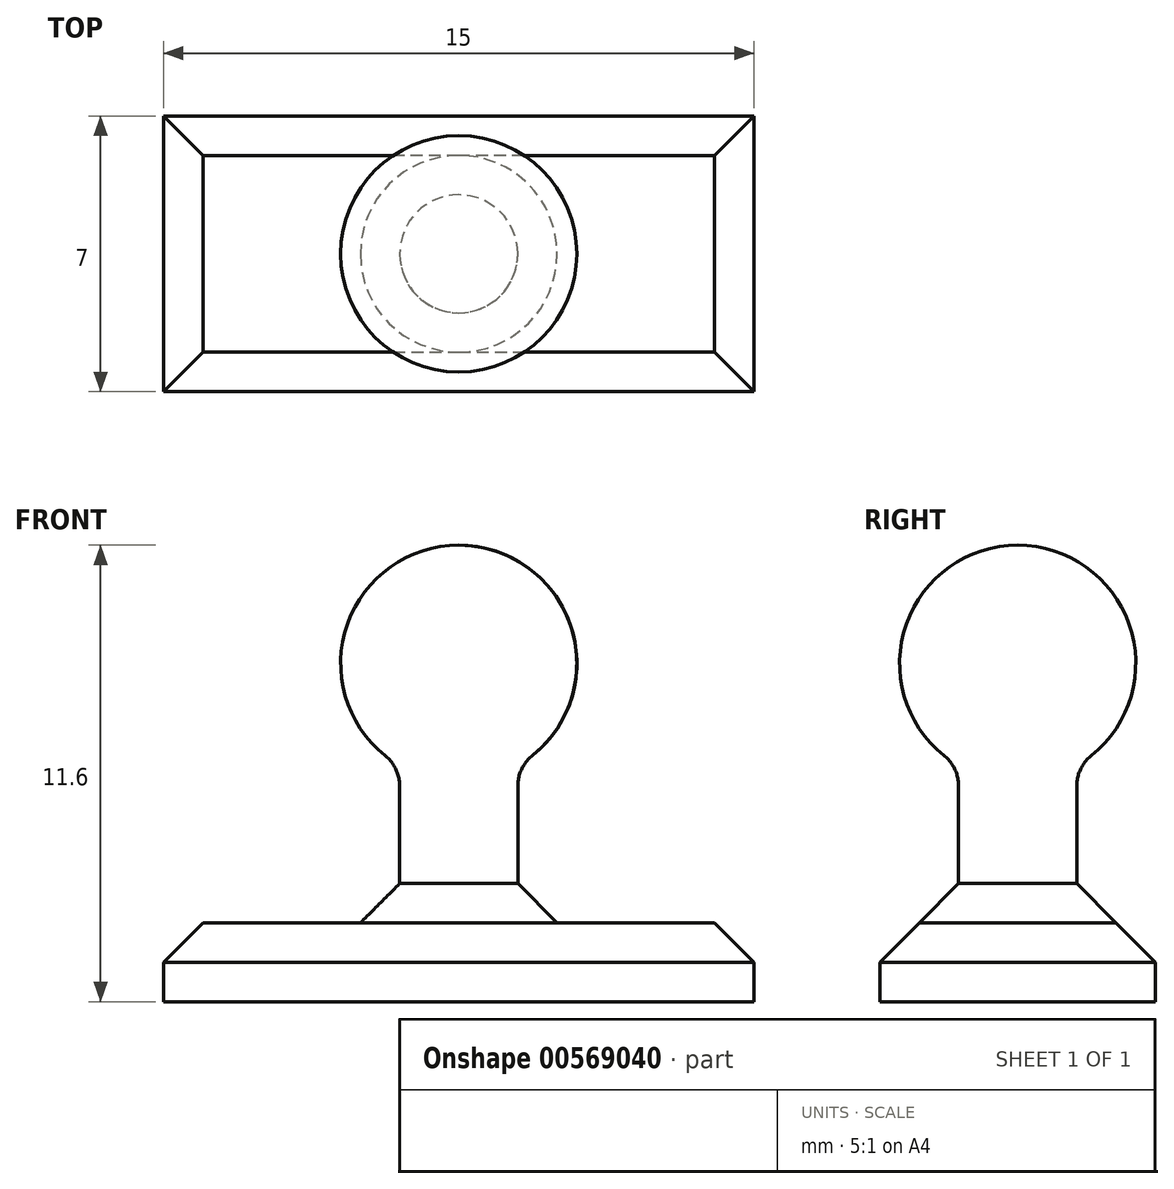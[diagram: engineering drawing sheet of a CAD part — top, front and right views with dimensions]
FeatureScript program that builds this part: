
annotation { "Feature Type Name" : "Feature", "Feature Type Description" : "" }
export const myFeature = defineFeature(function(context is Context, id is Id, definition is map)
    precondition{}
    {
        {
            var Q0;
            Q0=qCreatedBy(makeId("Front.planeOp"),FACE);
            var sketch = newSketch(context, id + "F0", { "sketchPlane" : qUnion([Q0])});
            skLineSegment(sketch, "E0", {"start": v(-1.5, 0) * mm, "end": v(-1.5, 4) * mm});
            skArc(sketch, "E1", {"start": v(0, 9.6) * mm, "mid": v(-2.9, 7.37) * mm, "end": v(-1.5, 4) * mm});
            skLineSegment(sketch, "E2", {"start": v(0, 0) * mm, "end": v(0, 9.6) * mm});
            skLineSegment(sketch, "E3", {"start": v(-1.5, 0) * mm, "end": v(0, 0) * mm});
            skLineSegment(sketch, "E4", {"start": v(0, 24.94) * mm, "end": v(0, -14.58) * mm, "construction": true});
            skSolve(sketch);
        }
        {
            var Q0;
            Q0=makeQuery(id+"F0.imprint","IMPRINT",FACE,{"disambiguationData":[TD([[makeQuery(id+"F0.imprint","IMPRINT",EDGE,{"derivedFrom":sQuery(id+"F0.wireOp",EDGE,"E0")}),-1.0]])]});
            var Q1;
            Q1=sQuery(id+"F0.wireOp",EDGE,"E3");
            var Q2;
            Q2=sQuery(id+"F0.wireOp",EDGE,"E0");
            var Q3;
            Q3=sQuery(id+"F0.wireOp",EDGE,"E1");
            var Q4;
            Q4=sQuery(id+"F0.wireOp",EDGE,"E2");
            revolve(context, id + "F1", {"entities" : qUnion([Q0]), "surfaceEntities" : qUnion([Q1, Q2, Q3]), "axis" : qUnion([Q4]), "revolveType" : RevolveType.FULL});
        }
        {
            var Q0;
            Q0=makeQuery(id+"F1.opRevolve","SWEPT_FACE",FACE,{"disambiguationData":[OSD([sQuery(id+"F0.wireOp",EDGE,"E3")])]});
            var sketch = newSketch(context, id + "F2", { "sketchPlane" : qUnion([Q0])});
            skLineSegment(sketch, "E5.bottom", {"start": v(7.5, 3.5) * mm, "end": v(-7.5, 3.5) * mm});
            skLineSegment(sketch, "E5.top", {"start": v(7.5, -3.5) * mm, "end": v(-7.5, -3.5) * mm});
            skLineSegment(sketch, "E5.left", {"start": v(7.5, 3.5) * mm, "end": v(7.5, -3.5) * mm});
            skLineSegment(sketch, "E5.right", {"start": v(-7.5, 3.5) * mm, "end": v(-7.5, -3.5) * mm});
            skPoint(sketch, "E5.middle", {"position": v(0, 0) * mm});
            skSolve(sketch);
        }
        {
            var Q0;
            Q0=makeQuery(id+"F2.imprint","IMPRINT",FACE,{"disambiguationData":[TD([[makeQuery(id+"F2.imprint","IMPRINT",EDGE,{"derivedFrom":sQuery(id+"F2.wireOp",EDGE,"E5.bottom")}),1.0]])]});
            var Q1;
            Q1=makeQuery(id+"F2.imprint","IMPRINT",FACE,{"disambiguationData":[TD([[makeQuery(id+"F2.imprint","IMPRINT",EDGE,{"derivedFrom":makeQuery(id+"F1.opRevolve","SWEPT_EDGE",EDGE,{"disambiguationData":[OSD([sQuery(id+"F0.wireOp",EDGE,"E0"),sQuery(id+"F0.wireOp",EDGE,"E3")])]})}),1.0]])]});
            extrude(context, id + "F3", {"entities" : qUnion([Q0, Q1]), "operationType" : NewBodyOperationType.ADD, "depth" : 2 * mm, "offsetDistance" : 25 * mm});
        }
        {
            var Q0;
            Q0=makeQuery(id+"F1.opRevolve","SWEPT_EDGE",EDGE,{"disambiguationData":[OSD([sQuery(id+"F0.wireOp",EDGE,"E0"),sQuery(id+"F0.wireOp",EDGE,"E3")])]});
            var Q1;
            Q1=makeQuery(id+"F1.opRevolve","SWEPT_EDGE",EDGE,{"disambiguationData":[OSD([sQuery(id+"F0.wireOp",EDGE,"E0"),sQuery(id+"F0.wireOp",EDGE,"E1")])]});
            fillet(context, id + "F4", {"entities" : qUnion([Q0, Q1]), "radius" : 1 * mm, "tangentPropagation" : true, "allowEdgeOverflow" : false});
        }
        {
            var Q0;
            Q0=makeQuery(id+"F3.opExtrude","CAP_FACE",FACE,{"disambiguationData":[OSD([sQuery(id+"F2.wireOp",EDGE,"E5.bottom"),sQuery(id+"F2.wireOp",EDGE,"E5.top"),sQuery(id+"F2.wireOp",EDGE,"E5.left"),sQuery(id+"F2.wireOp",EDGE,"E5.right")])],"isStart":true});
            chamfer(context, id + "F5", {"entities" : qUnion([Q0]), "width" : 1 * mm, "tangentPropagation" : true});
        }
    });
